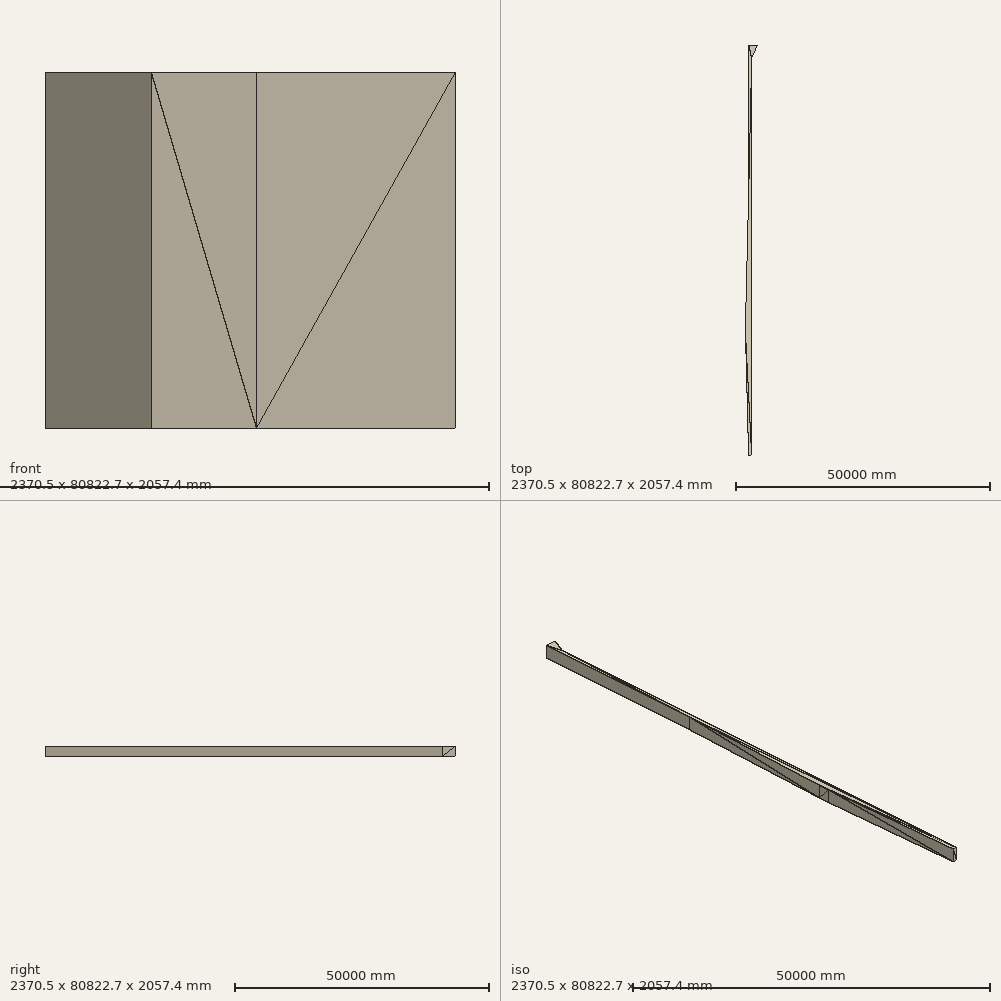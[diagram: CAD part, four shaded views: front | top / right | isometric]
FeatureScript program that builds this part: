
annotation { "Feature Type Name" : "Feature", "Feature Type Description" : "" }
export const myFeature = defineFeature(function(context is Context, id is Id, definition is map)
    precondition{}
    {
        {
            var Q0;
            Q0=qCreatedBy(makeId("Top.planeOp"),FACE);
            var sketch = newSketch(context, id + "F0", { "sketchPlane" : qUnion([Q0])});
            skLineSegment(sketch, "E0", {"start": v(1.37, 0) * mm, "end": v(-608.4, 0) * mm});
            skLineSegment(sketch, "E1", {"start": v(0, 0) * mm, "end": v(0, 78281.78) * mm});
            skLineSegment(sketch, "E2", {"start": v(0, 78281.78) * mm, "end": v(1150.02, 80822.72) * mm});
            skLineSegment(sketch, "E3", {"start": v(-575.23, 80822.72) * mm, "end": v(1150.02, 80822.72) * mm});
            skLineSegment(sketch, "E4", {"start": v(-575.23, 78281.78) * mm, "end": v(-575.23, 52368.46) * mm});
            skLineSegment(sketch, "E5", {"start": v(-575.23, 52368.46) * mm, "end": v(-1220.48, 25952.66) * mm});
            skLineSegment(sketch, "E6", {"start": v(-1220.48, 25952.66) * mm, "end": v(-1220.48, 24126.92) * mm});
            skLineSegment(sketch, "E7", {"start": v(-1220.48, 24126.92) * mm, "end": v(-608.4, 0) * mm});
            skLineSegment(sketch, "E8", {"start": v(-575.23, 78281.78) * mm, "end": v(-575.23, 80822.72) * mm});
            skSolve(sketch);
        }
        {
            var Q0;
            Q0 = qSketchRegion(id + "F0", true);
            extrude(context, id + "F1", {"entities" : qUnion([Q0]), "depth" : 2057.4 * mm, "offsetDistance" : 25.4 * mm});
        }
    });
